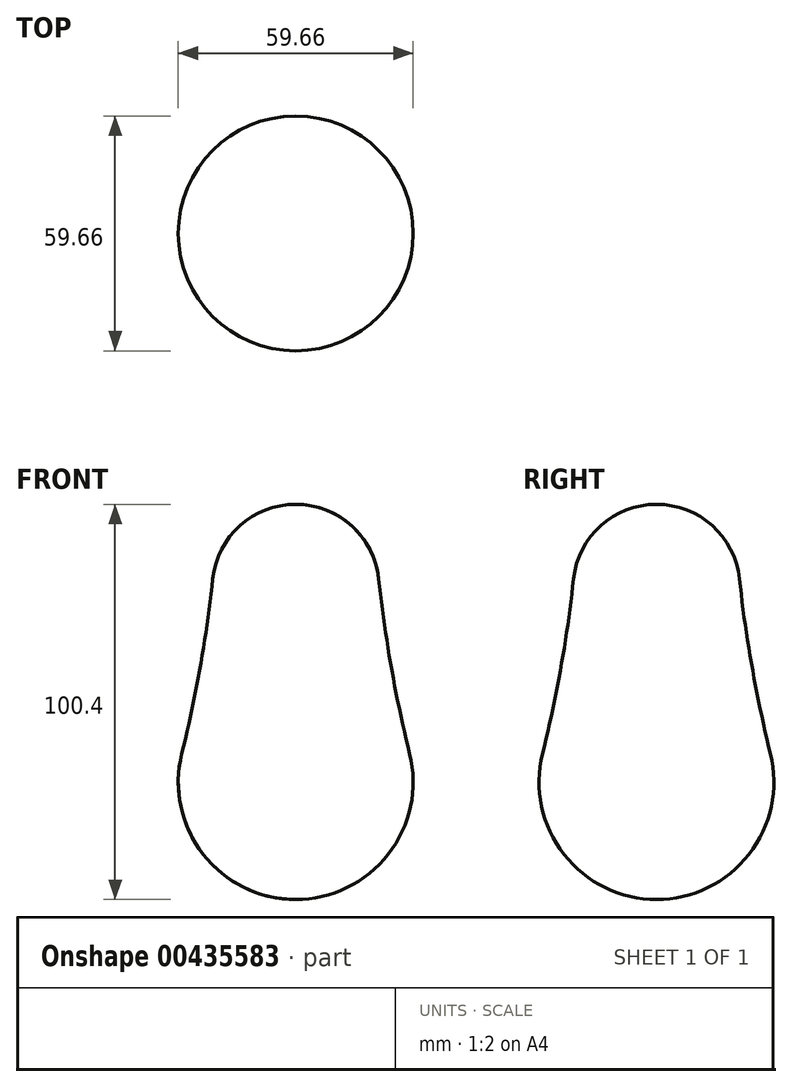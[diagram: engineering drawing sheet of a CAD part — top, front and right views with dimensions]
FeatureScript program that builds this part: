
annotation { "Feature Type Name" : "Feature", "Feature Type Description" : "" }
export const myFeature = defineFeature(function(context is Context, id is Id, definition is map)
    precondition{}
    {
        {
            var Q0;
            Q0=qCreatedBy(makeId("Front.planeOp"),FACE);
            var sketch = newSketch(context, id + "F0", { "sketchPlane" : qUnion([Q0])});
            skArc(sketch, "E0", {"start": v(0, 50.73) * mm, "mid": v(-14.17, 45.3) * mm, "end": v(-21.08, 31.8) * mm});
            skArc(sketch, "E1.MirrorCS", {"start": v(-21.08, 31.8) * mm, "mid": v(-24.26, 9.44) * mm, "end": v(-28.95, -12.64) * mm});
            skArc(sketch, "E2.MirrorC", {"start": v(0, -49.67) * mm, "mid": v(-23.5, -38.21) * mm, "end": v(-28.95, -12.64) * mm});
            skArc(sketch, "E3.MirrorC", {"start": v(-21.08, 31.8) * mm, "mid": v(-14.17, 45.3) * mm, "end": v(0, 50.73) * mm});
            skLineSegment(sketch, "E4", {"start": v(0, 59.05) * mm, "end": v(0, -54.1) * mm, "construction": true});
            skArc(sketch, "E5.trimOffspring", {"start": v(-28.95, -12.64) * mm, "mid": v(-23.5, -38.21) * mm, "end": v(0, -49.67) * mm});
            skLineSegment(sketch, "E6", {"start": v(0, 50.73) * mm, "end": v(0, -49.67) * mm});
            skPoint(sketch, "E7.orphan", {"position": v(21.08, 31.8) * mm});
            skPoint(sketch, "E8.orphan", {"position": v(28.95, -12.64) * mm});
            skSolve(sketch);
        }
        {
            var Q0;
            Q0 = qSketchRegion(id + "F0", true);
            var Q1;
            Q1=sQuery(id+"F0.wireOp",EDGE,"E6");
            revolve(context, id + "F1", {"entities" : qUnion([Q0]), "axis" : qUnion([Q1]), "revolveType" : RevolveType.FULL});
        }
    });
